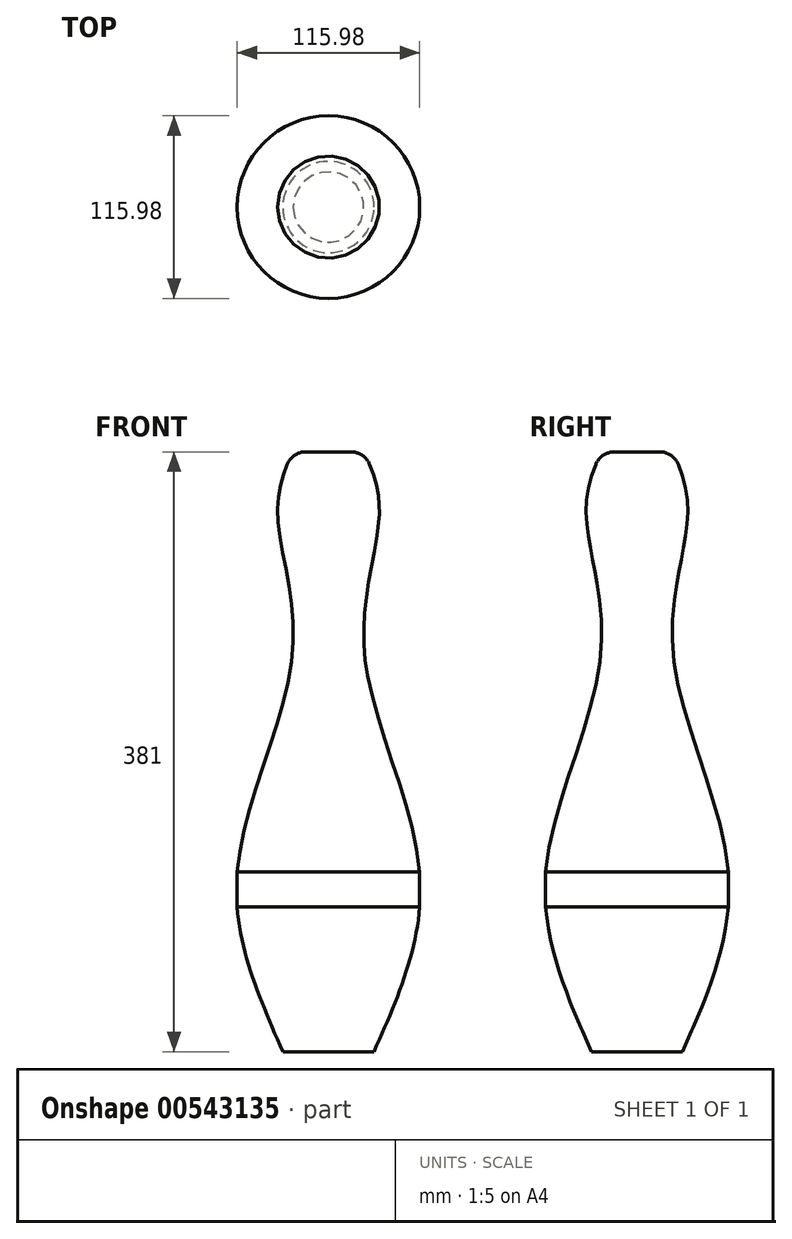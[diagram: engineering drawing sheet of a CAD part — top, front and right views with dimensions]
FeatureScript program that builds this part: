
annotation { "Feature Type Name" : "Feature", "Feature Type Description" : "" }
export const myFeature = defineFeature(function(context is Context, id is Id, definition is map)
    precondition{}
    {
        {
            var Q0;
            Q0=qCreatedBy(makeId("Front.planeOp"),FACE);
            var sketch = newSketch(context, id + "F0", { "sketchPlane" : qUnion([Q0])});
            skLineSegment(sketch, "E0.bottom", {"start": v(0, 0) * mm, "end": v(57.99, 0) * mm});
            skLineSegment(sketch, "E0.top", {"start": v(0, 381) * mm, "end": v(57.99, 381) * mm});
            skLineSegment(sketch, "E0.left", {"start": v(0, 0) * mm, "end": v(0, 381) * mm});
            skLineSegment(sketch, "E0.right", {"start": v(57.99, 92) * mm, "end": v(57.99, 114.3) * mm});
            skLineSegment(sketch, "E1.bottom", {"start": v(0, 0) * mm, "end": v(28.98, 0) * mm});
            skLineSegment(sketch, "E1.left", {"start": v(0, 0) * mm, "end": v(0, 114.3) * mm});
            skLineSegment(sketch, "E2.bottom", {"start": v(0, 0) * mm, "end": v(22.83, 0) * mm});
            skLineSegment(sketch, "E2.left", {"start": v(0, 0) * mm, "end": v(0, 254) * mm});
            skLineSegment(sketch, "E3.left", {"start": v(0, 0) * mm, "end": v(0, 342.9) * mm});
            skLineSegment(sketch, "E4", {"start": v(0, 0) * mm, "end": v(14.48, 0) * mm});
            skFitSpline(sketch, "E5", {"points": [v(28.98, 0) * mm, v(57.99, 114.3) * mm, v(22.83, 254) * mm, v(32.36, 342.9) * mm, v(22.83, 381) * mm], "startDerivative": vector(172.75, 391.35) * mm, "endDerivative": vector(-90.22, 212.05) * mm});
            skSolve(sketch);
        }
        {
            var Q0;
            {var subQ1=sQuery(id+"F0.wireOp",EDGE,"E0.left");Q0=makeQuery(id+"F0.imprint","IMPRINT",FACE,{"disambiguationData":[TD([[makeQuery(id+"F0.imprint","IMPRINT",EDGE,{"derivedFrom":subQ1}),-1.0]])]});}
            var Q1;
            Q1=sQuery(id+"F0.wireOp",EDGE,"E3.left");
            revolve(context, id + "F1", {"entities" : qUnion([Q0]), "axis" : qUnion([Q1]), "revolveType" : RevolveType.FULL});
        }
        {
            var Q0;
            Q0=makeQuery(id+"F1.opRevolve","SWEPT_EDGE",EDGE,{"disambiguationData":[OSD([sQuery(id+"F0.wireOp",EDGE,"E0.top"),sQuery(id+"F0.wireOp",EDGE,"E5")])]});
            fillet(context, id + "F2", {"entities" : qUnion([Q0]), "radius" : 12.7 * mm, "tangentPropagation" : true, "allowEdgeOverflow" : false});
        }
    });
